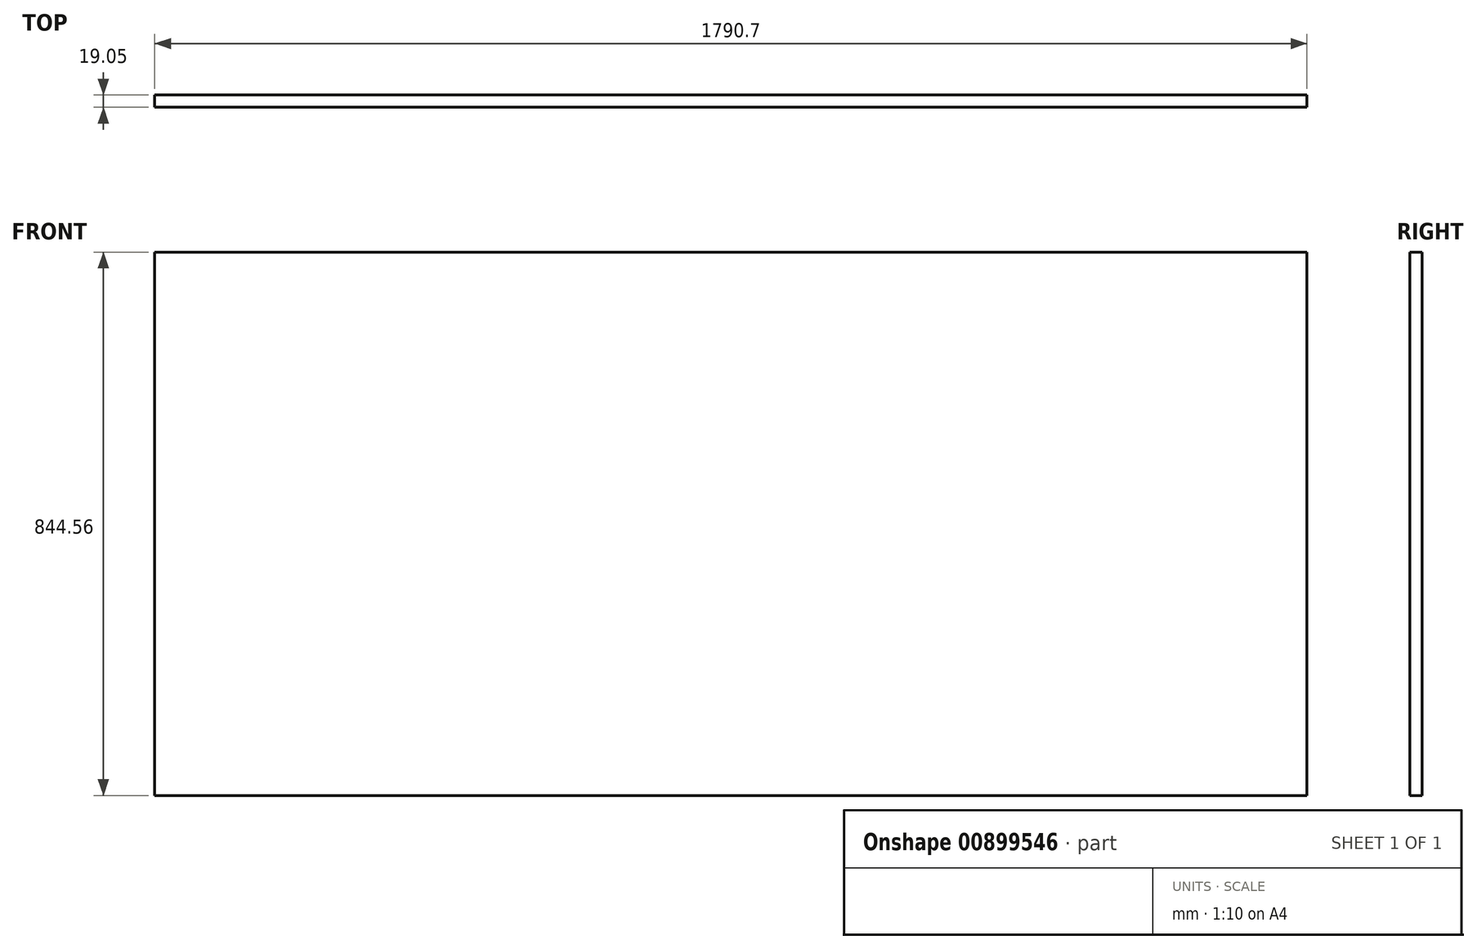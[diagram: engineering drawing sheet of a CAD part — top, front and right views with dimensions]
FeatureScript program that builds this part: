
annotation { "Feature Type Name" : "Feature", "Feature Type Description" : "" }
export const myFeature = defineFeature(function(context is Context, id is Id, definition is map)
    precondition{}
    {
        {
            var Q0;
            Q0=qCreatedBy(makeId("Front.planeOp"),FACE);
            var sketch = newSketch(context, id + "F0", { "sketchPlane" : qUnion([Q0])});
            skLineSegment(sketch, "E0.bottom", {"start": v(-895.35, 422.28) * mm, "end": v(895.35, 422.28) * mm});
            skLineSegment(sketch, "E0.top", {"start": v(-895.35, -422.28) * mm, "end": v(895.35, -422.28) * mm});
            skLineSegment(sketch, "E0.left", {"start": v(-895.35, 422.28) * mm, "end": v(-895.35, -422.28) * mm});
            skLineSegment(sketch, "E0.right", {"start": v(895.35, 422.28) * mm, "end": v(895.35, -422.28) * mm});
            skPoint(sketch, "E0.middle", {"position": v(0, 0) * mm});
            skSolve(sketch);
        }
        {
            var Q0;
            Q0=makeQuery(id+"F0.imprint","IMPRINT",FACE,{"disambiguationData":[TD([[makeQuery(id+"F0.imprint","IMPRINT",EDGE,{"derivedFrom":sQuery(id+"F0.wireOp",EDGE,"E0.bottom")}),-1.0]])]});
            extrude(context, id + "F1", {"entities" : qUnion([Q0]), "depth" : 19.05 * mm, "offsetDistance" : 25.4 * mm});
        }
    });
